# Revit family: Block 600 (10.24)
name_source: partatom
category: Оборудование
units: mm (PartAtom-declared; Revit-internal decimal feet)

## family parameters
Всегда вертикально = Да
Классификация = Нет
На основе рабочей плоскости = Нет
Общий = Нет
При загрузке вырезать с полостями = Нет
Размер круглого соединителя = Использовать диаметр
Тип детали = Нормальный
Точка расчета площади = Нет

## types (1)
- Block 600
    ADSK_Единица измерения = шт.
    ADSK_Завод-изготовитель = ООО «Турков»
    ADSK_Количество = 1
    ADSK_Количество фаз = 1
    ADSK_Марка = Block 600
    ADSK_Наименование = Канальный очиститель с высокой фильтрацией воздуха
    ADSK_Напряжение = 220 В
    ADSK_Номинальная мощность = 320 Вт
    ADSK_Расход воздуха приточный = 600.0 м³/ч
    ADSK_Свободный напор воздуха = 50.0 Па
    ADSK_Ток = 1 А
    К Высота = 560 мм
    К Глубина = 339 мм
    К Длина = 942 мм
    К Стенка Толщина = 51 мм
    КА Высота = 43 мм
    КА Длина = 85 мм
    КА Отступ = 50 мм
    КА Ширина = 85 мм
    КА отступ 2 = 80 мм
    Материал КА = Материал КА
    Материал СЗ = Материал СЗ
    Материал корпуса = Материал ПУ
    Материал креплений = Материал Кр
    Материал патрубков = Материал Па
    П Диаметр = 200 мм
    П Длина = 45 мм
    П Отступ снизу = 163 мм
    Ф СЗ = 350 мм
